# Revit family: CARLO CYLINDER LIGHT WALL MOUNT
name_source: partatom
category: Lighting Fixtures
units: mm (PartAtom-declared; Revit-internal decimal feet)

## family parameters
Cut with Voids When Loaded = No
Host = Face
Light Source = Yes
Part Type = Normal
Room Calculation Point = No
Round Connector Dimension = Use Diameter
Shared = No

## types (9) — shared parameters
Average life based on L70(HRS) = 100000
BOTTOM LENGTH = 0' - 4 17/32"
BOTTOM LENGTH 1 = 0' - 2 1/2"
BOTTOM WIDTH = 0' - 4 17/32"
BOTTOM WIDTH 1 = 0' - 3 1/32"
Body Material = BLACK
CRI = 90Ra
Color Filter = 16777215
Default Elevation = 4' - 0"
Description = This architectural Carlo Cylinder light is designed for accent lighting and features a state-of-the-art
design.
Dimming / Control = 10 V
Dimming Lamp Color Temperature Shift = <None>
GLASS = Glass
IP Rating = 65
Load Classification = Lighting
Manufacturer = Above All Lighting
Power Factor = 0.9
Tilt Angle = 180.00°
Type Comments = CARLO CYLINDER LIGHT  Wall Mount
URL = https://www.abovealllighting.com
Voltage = 120 V
Voltage_Input = 0 V

## per-type parameters (varying)
| type | Apparent Load | BEAMING ANGLE | Base Curve | Curve base Height | FIXED END HEIGHT | LIGHT DIA | LIGHT LENGTH | LIGHT PLACEMENT | LIGHT RADIUS | Light Length 1 | Photometric Web File | Wattage Comments | Wattage_Input |
| CCL6-13-35SPSW8-PC-60-WM-BK | 44 VA | 60.00° | 0' - 2 11/16" | 0' - 2 27/32" | 0' - 8 13/32" | 0' - 6" | 1' - 1" | 0' - 5 13/32" | 0' - 3" | 0' - 4 11/32" | CCL6 35W 3000K 60° (up and down light).IES | 22W/29W/35W | 35 W |
| CCL4-11-20SPSW8-PC-60-WM-BK | 25 VA | 60.00° | 0' - 2" | 0' - 3 1/8" | 0' - 6 13/32" | 0' - 4" | 0' - 11 1/32" | 0' - 4 13/32" | 0' - 2" | 0' - 3 11/16" | CCL4 20W 3000K 60° (up and down light).IES | 12W/16W/20W | 20 W |
| CCL3-09-10SPSW8-PC-60-WM-BK | 13 VA | 60.00° | 0' - 1 19/32" | 0' - 3 1/2" | 0' - 5 13/32" | 0' - 3" | 0' - 8 31/32" | 0' - 3 29/32" | 0' - 1 1/2" | 0' - 3" | CCL3 10W 3000K 60° (up and down light).IES | 6W/8W/10W | 10 W |
| CCL3-09-10SPSW8-PC-25-WM-BK | 13 VA | 25.00° | 0' - 1 19/32" | 0' - 3 1/2" | 0' - 5 13/32" | 0' - 3" | 0' - 8 31/32" | 0' - 3 29/32" | 0' - 1 1/2" | 0' - 3" | CCL3 10W 3000K 25° (up and down light).IES | 6W/8W/10W | 10 W |
| CCL3-09-10SPSW8-PC-40-WM-BK | 13 VA | 40.00° | 0' - 1 19/32" | 0' - 3 1/2" | 0' - 5 13/32" | 0' - 3" | 0' - 8 31/32" | 0' - 3 29/32" | 0' - 1 1/2" | 0' - 3" | CCL3 10W 3000K 40° (up and down light).IES | 6W/8W/10W | 10 W |
| CCL4-11-20SPSW8-PC-25-WM-BK | 25 VA | 25.00° | 0' - 2" | 0' - 3 1/8" | 0' - 6 13/32" | 0' - 4" | 0' - 11 1/32" | 0' - 4 13/32" | 0' - 2" | 0' - 3 11/16" | CCL4 20W 3000K 25° (up and down light).IES | 12W/16W/20W | 20 W |
| CCL4-11-20SPSW8-PC-40-WM-BK | 25 VA | 40.00° | 0' - 2" | 0' - 3 1/8" | 0' - 6 13/32" | 0' - 4" | 0' - 11 1/32" | 0' - 4 13/32" | 0' - 2" | 0' - 3 11/16" | CCL4 20W 3000K 40° (up and down light).IES | 12W/16W/20W | 20 W |
| CCL6-13-35SPSW8-PC-25-WM-BK | 44 VA | 25.00° | 0' - 2 11/16" | 0' - 2 27/32" | 0' - 8 13/32" | 0' - 6" | 1' - 1" | 0' - 5 13/32" | 0' - 3" | 0' - 4 11/32" | CCL6 35W 3000K 25° (up and down light).IES | 22W/29W/35W | 35 W |
| CCL6-13-35SPSW8-PC-40-WM-BK | 44 VA | 40.00° | 0' - 2 11/16" | 0' - 2 27/32" | 0' - 8 13/32" | 0' - 6" | 1' - 1" | 0' - 5 13/32" | 0' - 3" | 0' - 4 11/32" | CCL6 35W 3000K 40° (up and down light).IES | 22W/29W/35W | 35 W |

note: column(s) folded — value = type name in every type: Model

## geometry (parser evidence)
native form markers: Sweep x8
no freeform markers — native parametric forms only
